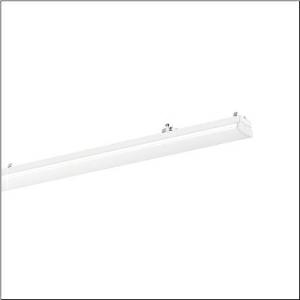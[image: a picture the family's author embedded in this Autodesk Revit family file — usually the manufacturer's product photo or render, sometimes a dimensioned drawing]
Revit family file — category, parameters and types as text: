
# Revit family: licross_r__21_recessed_opal_mo_52te1dcn485g_36e8
name_source: partatom
category: Lighting Fixtures
units: mm (PartAtom-declared; Revit-internal decimal feet)

## family parameters
Cut with Voids When Loaded = No
Host = Face
Light Source = No
Part Type = Normal
Room Calculation Point = No
Round Connector Dimension = Use Diameter
Shared = No

## types (1)
- --- (1 x LED, 8780 lm, 49.9 W, 4000K)
    Apparent Load = 50 VA
    CIE Flux Codes = 44 73 91 87 100
    Color Rendering = 80
    Color Temperature = 4000K
    Default Elevation = 1800 mm
    Description = Licross® 21 recessed opal MO, luminaire insert, of sheet steel, galvanised, coil coated, white, length: 1.500mm, width: 66mm, height: 67mm, LED rated luminous flux: 8.780lm, light colour: 840, control gear: ON/OFF Multilumen, CLOi, with plug, 3-pole, with phase selection, mains connection: 220..240V, AC, 50/60Hz, start of lifetime: 50W, end of service life: 61W, halogen-free wiring, primary optical cover: cover, of PMMA, light emission: direct with ceiling illumination distribution, primary light characteristic: symmetric, protection rating (complete): IP54, insulation class (complete): insulation class I (protective earthing), certification: CE, ENEC, VDE, UKCA, protection symbol: D if used in an environment with non-conductive dust loads with corresponding accessories, impact resistance: IK06, permissible ambient temperature for indoor applications: -35..+40°C, corresponds to IFS (International Featured Standards) requirements for safety and quality in the food industry, reducing of maximum allowable ambient temperature of 5°C with ceiling mounting, LABS conformity tested according to VDMA 24364:2018-05, packaging unit: 1 piece
    Height = 83 mm
    Lamp = 1 x LED
    Lamp Light Flux = 8780 lm
    Lamp Power = 49.9 W
    Lamp count = 1
    Length = 1500 mm
    Luminous efficacy = 176 lm/W
    Manufacturer = Siteco
    ModVariant = No
    Model = 52TE1DCN485G
    Mounting Place = Ceiling
    Mounting Type = Pendant
    Number of Poles = 1
    OnlyDefault = Yes
    Power Factor = 1
    Product Name = Licross® 21 recessed opal MO
    Product group = luminaire insert
    ProductGroupID = 902
    Protection Class = Protection class I
    Protection Degree = IP 54
    RLX_Detail_Level = 1
    RLX_Emergency_Light_Flux = 0 lm
    RLX_Emergency_Type = 0
    RLX_Emergency_Type_DB = No
    RlxData = <blob elided: 24605 chars, md5=4b24afb3>
    Socket = socket
    Standby Power = 0 W
    System Light Flux = 8780 lm
    System Power = 50 W
    Type Comments = factory setting: luminous flux: 100 % | (A | C | E) | 116 mA
    Type Image = l_1313666.jpg
    URL = http://relux.com
    VarID = @adj_068522
    Voltage = 0 V
    Weight = 0.00 kg
    Width = 76 mm

## geometry (parser evidence)
native form markers: Blend x4, Sweep x13
no freeform markers — native parametric forms only
